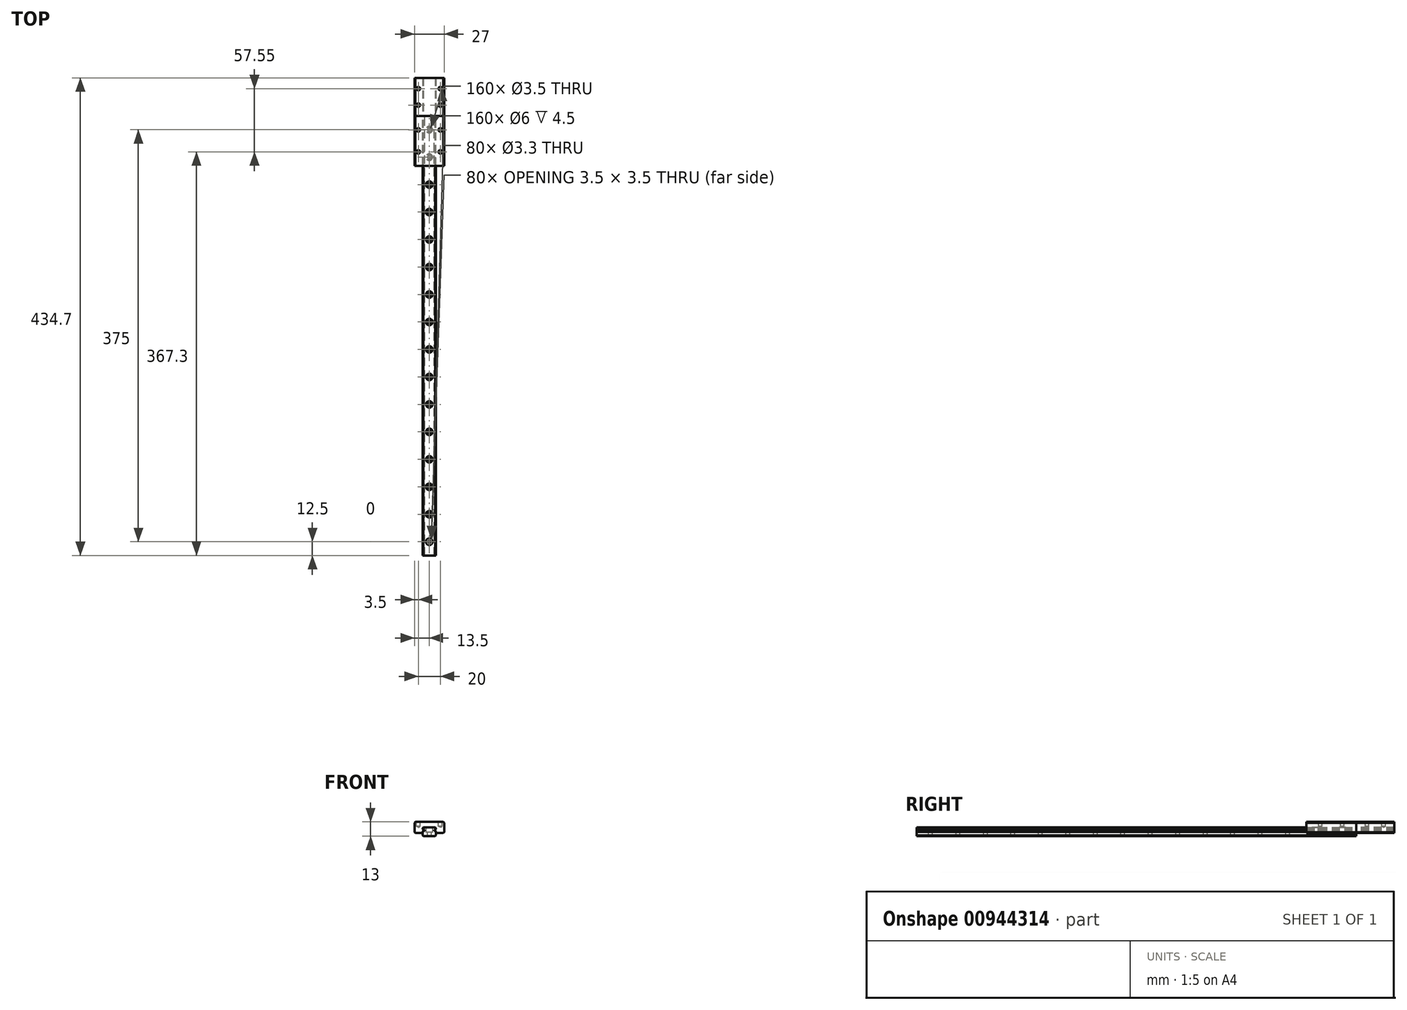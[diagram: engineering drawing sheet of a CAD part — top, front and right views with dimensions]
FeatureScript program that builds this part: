
annotation { "Feature Type Name" : "Feature", "Feature Type Description" : "" }
export const myFeature = defineFeature(function(context is Context, id is Id, definition is map)
    precondition{}
    {
        {
            var Q0;
            Q0=qCreatedBy(makeId("Front.planeOp"),FACE);
            var sketch = newSketch(context, id + "F0", { "sketchPlane" : qUnion([Q0])});
            skLineSegment(sketch, "E0.bottom", {"start": v(5.3, -4) * mm, "end": v(-5.3, -4) * mm});
            skLineSegment(sketch, "E0.top", {"start": v(5.3, 4) * mm, "end": v(-5.3, 4) * mm});
            skLineSegment(sketch, "E0.left", {"start": v(6, -3.3) * mm, "end": v(6, 0.09) * mm});
            skLineSegment(sketch, "E0.right", {"start": v(-6, -3.3) * mm, "end": v(-6, 0.09) * mm});
            skPoint(sketch, "E0.middle", {"position": v(0, 0) * mm});
            skLineSegment(sketch, "E1", {"start": v(0, 12.36) * mm, "end": v(0, -9.73) * mm, "construction": true});
            skLineSegment(sketch, "E2", {"start": v(-6, 2.5) * mm, "end": v(-5.3, 1.8) * mm});
            skLineSegment(sketch, "E3", {"start": v(-5.3, 1.8) * mm, "end": v(-4.3, 1.8) * mm});
            skLineSegment(sketch, "E4", {"start": v(-4.3, 1.8) * mm, "end": v(-4.3, 0.8) * mm});
            skLineSegment(sketch, "E5", {"start": v(-4.3, 0.8) * mm, "end": v(-5.3, 0.8) * mm});
            skLineSegment(sketch, "E6", {"start": v(-5.3, 0.8) * mm, "end": v(-6, 0.09) * mm});
            skLineSegment(sketch, "E7.MirrorCS", {"start": v(4.3, 0.8) * mm, "end": v(5.3, 0.8) * mm});
            skLineSegment(sketch, "E8.MirrorCS", {"start": v(5.3, 0.8) * mm, "end": v(6, 0.09) * mm});
            skLineSegment(sketch, "E9.MirrorCS", {"start": v(4.3, 1.8) * mm, "end": v(4.3, 0.8) * mm});
            skLineSegment(sketch, "E10.MirrorCS", {"start": v(6, 2.5) * mm, "end": v(5.3, 1.8) * mm});
            skLineSegment(sketch, "E11.MirrorCS", {"start": v(5.3, 1.8) * mm, "end": v(4.3, 1.8) * mm});
            skLineSegment(sketch, "E12.trimOffspring", {"start": v(-6, 2.5) * mm, "end": v(-6, 3.3) * mm});
            skLineSegment(sketch, "E13.trimOffspring", {"start": v(6, 2.5) * mm, "end": v(6, 3.3) * mm});
            skLineSegment(sketch, "E14", {"start": v(-6, 3.3) * mm, "end": v(-5.3, 4) * mm});
            skLineSegment(sketch, "E15.MirrorCS", {"start": v(6, 3.3) * mm, "end": v(5.3, 4) * mm});
            skLineSegment(sketch, "E16.MirrorCS", {"start": v(-6, -3.3) * mm, "end": v(-5.3, -4) * mm});
            skLineSegment(sketch, "E17.MirrorCS", {"start": v(6, -3.3) * mm, "end": v(5.3, -4) * mm});
            skPoint(sketch, "E18.orphan", {"position": v(-6, 4) * mm});
            skPoint(sketch, "E19.orphan", {"position": v(6, 4) * mm});
            skPoint(sketch, "E20.orphan", {"position": v(6, -4) * mm});
            skPoint(sketch, "E21.orphan", {"position": v(-6, -4) * mm});
            skSolve(sketch);
        }
        {
            var Q0;
            Q0=makeQuery(id+"F0.imprint","IMPRINT",FACE,{"disambiguationData":[TD([[makeQuery(id+"F0.imprint","IMPRINT",EDGE,{"derivedFrom":sQuery(id+"F0.wireOp",EDGE,"E0.bottom")}),-1.0]])]});
            extrude(context, id + "F1", {"entities" : qUnion([Q0]), "depth" : 400 * mm, "offsetDistance" : 25 * mm});
        }
        {
            var Q0;
            Q0=makeQuery(id+"F1.opExtrude","SWEPT_FACE",FACE,{"disambiguationData":[OSD([sQuery(id+"F0.wireOp",EDGE,"E0.top")])]});
            var sketch = newSketch(context, id + "F2", { "sketchPlane" : qUnion([Q0])});
            skLineSegment(sketch, "E22", {"start": v(0, 4.61) * mm, "end": v(0, -375.08) * mm, "construction": true});
            skCircle(sketch, "E23", {"center": v(0, -12.5) * mm, "radius": 1.75 * mm});
            skCircle(sketch, "E24.1.0.0", {"center": v(0, -37.5) * mm, "radius": 1.75 * mm});
            skCircle(sketch, "E24.2.0.0", {"center": v(0, -62.5) * mm, "radius": 1.75 * mm});
            skCircle(sketch, "E24.3.0.0", {"center": v(0, -87.5) * mm, "radius": 1.75 * mm});
            skCircle(sketch, "E24.4.0.0", {"center": v(0, -112.5) * mm, "radius": 1.75 * mm});
            skCircle(sketch, "E24.5.0.0", {"center": v(0, -137.5) * mm, "radius": 1.75 * mm});
            skCircle(sketch, "E24.6.0.0", {"center": v(0, -162.5) * mm, "radius": 1.75 * mm});
            skCircle(sketch, "E24.7.0.0", {"center": v(0, -187.5) * mm, "radius": 1.75 * mm});
            skCircle(sketch, "E24.8.0.0", {"center": v(0, -212.5) * mm, "radius": 1.75 * mm});
            skLineSegment(sketch, "E24.direction1", {"start": v(0, -12.5) * mm, "end": v(0, -37.5) * mm, "construction": true});
            skCircle(sketch, "E25.0.9.0", {"center": v(0, -237.5) * mm, "radius": 1.75 * mm});
            skCircle(sketch, "E25.0.10.0", {"center": v(0, -262.5) * mm, "radius": 1.75 * mm});
            skCircle(sketch, "E25.0.11.0", {"center": v(0, -287.5) * mm, "radius": 1.75 * mm});
            skCircle(sketch, "E25.0.12.0", {"center": v(0, -312.5) * mm, "radius": 1.75 * mm});
            skCircle(sketch, "E25.0.13.0", {"center": v(0, -337.5) * mm, "radius": 1.75 * mm});
            skCircle(sketch, "E26.0.14.0", {"center": v(0, -362.5) * mm, "radius": 1.75 * mm});
            skCircle(sketch, "E26.0.15.0", {"center": v(0, -387.5) * mm, "radius": 1.75 * mm});
            skSolve(sketch);
        }
        {
            var Q0;
            Q0=qSketchRegion(id+"F2",true);
            extrude(context, id + "F3", {"entities" : qUnion([Q0]), "operationType" : NewBodyOperationType.REMOVE, "endBound" : BoundingType.THROUGH_ALL, "oppositeDirection" : true, "depth" : 25 * mm, "offsetDistance" : 25 * mm});
        }
        {
            var Q0;
            Q0=makeQuery(id+"F1.opExtrude","SWEPT_FACE",FACE,{"disambiguationData":[OSD([sQuery(id+"F0.wireOp",EDGE,"E0.top")])]});
            var sketch = newSketch(context, id + "F4", { "sketchPlane" : qUnion([Q0])});
            skLineSegment(sketch, "E27", {"start": v(0, 167.82) * mm, "end": v(0, -211.88) * mm, "construction": true});
            skCircle(sketch, "E28", {"center": v(0, -12.5) * mm, "radius": 3 * mm});
            skCircle(sketch, "E29.1.0.0", {"center": v(0, -37.5) * mm, "radius": 3 * mm});
            skCircle(sketch, "E29.2.0.0", {"center": v(0, -62.5) * mm, "radius": 3 * mm});
            skCircle(sketch, "E29.3.0.0", {"center": v(0, -87.5) * mm, "radius": 3 * mm});
            skCircle(sketch, "E29.4.0.0", {"center": v(0, -112.5) * mm, "radius": 3 * mm});
            skCircle(sketch, "E29.5.0.0", {"center": v(0, -137.5) * mm, "radius": 3 * mm});
            skCircle(sketch, "E29.6.0.0", {"center": v(0, -162.5) * mm, "radius": 3 * mm});
            skCircle(sketch, "E29.7.0.0", {"center": v(0, -187.5) * mm, "radius": 3 * mm});
            skCircle(sketch, "E29.8.0.0", {"center": v(0, -212.5) * mm, "radius": 3 * mm});
            skLineSegment(sketch, "E29.direction1", {"start": v(0, -12.5) * mm, "end": v(0, -37.5) * mm, "construction": true});
            skCircle(sketch, "E30.0.9.0", {"center": v(0, -237.5) * mm, "radius": 3 * mm});
            skCircle(sketch, "E30.0.10.0", {"center": v(0, -262.5) * mm, "radius": 3 * mm});
            skCircle(sketch, "E30.0.11.0", {"center": v(0, -287.5) * mm, "radius": 3 * mm});
            skCircle(sketch, "E30.0.12.0", {"center": v(0, -312.5) * mm, "radius": 3 * mm});
            skCircle(sketch, "E30.0.13.0", {"center": v(0, -337.5) * mm, "radius": 3 * mm});
            skCircle(sketch, "E31.0.14.0", {"center": v(0, -362.5) * mm, "radius": 3 * mm});
            skCircle(sketch, "E31.0.15.0", {"center": v(0, -387.5) * mm, "radius": 3 * mm});
            skSolve(sketch);
        }
        {
            var Q0;
            Q0=qSketchRegion(id+"F4",true);
            extrude(context, id + "F5", {"entities" : qUnion([Q0]), "operationType" : NewBodyOperationType.REMOVE, "oppositeDirection" : true, "depth" : 4.5 * mm, "offsetDistance" : 25 * mm});
        }
        {
            var Q0;
            Q0=qCreatedBy(makeId("Front.planeOp"),FACE);
            var sketch = newSketch(context, id + "F6", { "sketchPlane" : qUnion([Q0])});
            skLineSegment(sketch, "E32", {"start": v(-6.15, -1) * mm, "end": v(-12.8, -1) * mm});
            skLineSegment(sketch, "E33", {"start": v(-13.5, -0.3) * mm, "end": v(-13.5, 8.3) * mm});
            skLineSegment(sketch, "E34", {"start": v(-12.8, 9) * mm, "end": v(0, 9) * mm});
            skLineSegment(sketch, "E35", {"start": v(-6.15, -1) * mm, "end": v(-6.15, 0.15) * mm});
            skLineSegment(sketch, "E36", {"start": v(-6.15, 0.15) * mm, "end": v(-5.3, 1) * mm});
            skLineSegment(sketch, "E37", {"start": v(-5.3, 1) * mm, "end": v(-5.3, 1.58) * mm});
            skLineSegment(sketch, "E38", {"start": v(-5.3, 1.58) * mm, "end": v(-6.15, 2.44) * mm});
            skLineSegment(sketch, "E39", {"start": v(-6.15, 2.44) * mm, "end": v(-6.15, 3.36) * mm});
            skLineSegment(sketch, "E40", {"start": v(-6.15, 3.36) * mm, "end": v(-5.36, 4.15) * mm});
            skLineSegment(sketch, "E41", {"start": v(-5.36, 4.15) * mm, "end": v(0, 4.15) * mm});
            skLineSegment(sketch, "E42", {"start": v(-13.5, 8.3) * mm, "end": v(-12.8, 9) * mm});
            skLineSegment(sketch, "E43", {"start": v(-12.8, -1) * mm, "end": v(-13.5, -0.3) * mm});
            skPoint(sketch, "E44.orphan", {"position": v(-13.5, -1) * mm});
            skPoint(sketch, "E45.orphan", {"position": v(-13.5, 9) * mm});
            skLineSegment(sketch, "E46.MirrorCS", {"start": v(12.8, 9) * mm, "end": v(0, 9) * mm});
            skLineSegment(sketch, "E47.MirrorCS", {"start": v(13.5, 8.3) * mm, "end": v(12.8, 9) * mm});
            skLineSegment(sketch, "E48.MirrorCS", {"start": v(13.5, -0.3) * mm, "end": v(13.5, 8.3) * mm});
            skLineSegment(sketch, "E49.MirrorCS", {"start": v(12.8, -1) * mm, "end": v(13.5, -0.3) * mm});
            skLineSegment(sketch, "E50.MirrorCS", {"start": v(6.15, -1) * mm, "end": v(12.8, -1) * mm});
            skLineSegment(sketch, "E51.MirrorCS", {"start": v(6.15, -1) * mm, "end": v(6.15, 0.15) * mm});
            skLineSegment(sketch, "E52.MirrorCS", {"start": v(6.15, 0.15) * mm, "end": v(5.3, 1) * mm});
            skLineSegment(sketch, "E53.MirrorCS", {"start": v(5.3, 1) * mm, "end": v(5.3, 1.58) * mm});
            skLineSegment(sketch, "E54.MirrorCS", {"start": v(5.3, 1.58) * mm, "end": v(6.15, 2.44) * mm});
            skLineSegment(sketch, "E55.MirrorCS", {"start": v(6.15, 2.44) * mm, "end": v(6.15, 3.36) * mm});
            skLineSegment(sketch, "E56.MirrorCS", {"start": v(6.15, 3.36) * mm, "end": v(5.36, 4.15) * mm});
            skLineSegment(sketch, "E57.MirrorCS", {"start": v(5.36, 4.15) * mm, "end": v(0, 4.15) * mm});
            skSolve(sketch);
        }
        {
            var Q0;
            Q0=qSketchRegion(id+"F6",true);
            extrude(context, id + "F7", {"entities" : qUnion([Q0]), "depth" : 45.4 * mm, "offsetDistance" : 25 * mm});
        }
        {
            var Q0;
            Q0=qSketchRegion(id+"F6",true);
            extrude(context, id + "F8", {"entities" : qUnion([Q0]), "oppositeDirection" : true, "depth" : 34.7 * mm, "offsetDistance" : 25 * mm});
        }
        {
            var Q0;
            Q0=makeQuery(id+"F7.opExtrude","SWEPT_FACE",FACE,{"disambiguationData":[OSD([sQuery(id+"F6.wireOp",EDGE,"E34"),sQuery(id+"F6.wireOp",EDGE,"E46.MirrorCS")])]});
            var sketch = newSketch(context, id + "F9", { "sketchPlane" : qUnion([Q0])});
            skLineSegment(sketch, "E58", {"start": v(-12.8, 0) * mm, "end": v(12.8, -45.4) * mm, "construction": true});
            skLineSegment(sketch, "E59", {"start": v(12.8, 0) * mm, "end": v(-12.8, -45.4) * mm, "construction": true});
            skLineSegment(sketch, "E60", {"start": v(-37.81, -22.7) * mm, "end": v(32.35, -22.7) * mm, "construction": true});
            skPoint(sketch, "E60.startSnap0", {"position": v(0, -22.7) * mm});
            skLineSegment(sketch, "E61", {"start": v(0, 0) * mm, "end": v(0, -61.52) * mm, "construction": true});
            skCircle(sketch, "E62", {"center": v(-10, -12.7) * mm, "radius": 1.5 * mm});
            skCircle(sketch, "E63.MirrorC", {"center": v(10, -12.7) * mm, "radius": 1.5 * mm});
            skCircle(sketch, "E64.MirrorC", {"center": v(-10, -32.7) * mm, "radius": 1.5 * mm});
            skCircle(sketch, "E65.MirrorC", {"center": v(10, -32.7) * mm, "radius": 1.5 * mm});
            skSolve(sketch);
        }
        {
            var Q0;
            Q0=makeQuery(id+"F8.opExtrude","SWEPT_FACE",FACE,{"disambiguationData":[OSD([sQuery(id+"F6.wireOp",EDGE,"E34"),sQuery(id+"F6.wireOp",EDGE,"E46.MirrorCS")])]});
            var sketch = newSketch(context, id + "F10", { "sketchPlane" : qUnion([Q0])});
            skLineSegment(sketch, "E66", {"start": v(-34.35, 17.35) * mm, "end": v(28.23, 17.35) * mm, "construction": true});
            skLineSegment(sketch, "E67", {"start": v(0, 49.38) * mm, "end": v(0, -1.77) * mm, "construction": true});
            skCircle(sketch, "E68", {"center": v(-10, 24.85) * mm, "radius": 1.5 * mm});
            skCircle(sketch, "E69.MirrorC", {"center": v(10, 24.85) * mm, "radius": 1.5 * mm});
            skCircle(sketch, "E70.MirrorC", {"center": v(-10, 9.85) * mm, "radius": 1.5 * mm});
            skCircle(sketch, "E71.MirrorC", {"center": v(10, 9.85) * mm, "radius": 1.5 * mm});
            skSolve(sketch);
        }
        {
            var Q0;
            Q0=sQuery(id+"F9.wireOp",VERTEX,"E62.center");
            var Q1;
            Q1=sQuery(id+"F9.wireOp",VERTEX,"E63.MirrorC.center");
            var Q2;
            Q2=sQuery(id+"F9.wireOp",VERTEX,"E64.MirrorC.center");
            var Q3;
            Q3=sQuery(id+"F9.wireOp",VERTEX,"E65.MirrorC.center");
            var Q4;
            Q4=makeQuery(id+"F7.opExtrude","SWEPT_BODY",BODY,{"disambiguationData":[OSD([sQuery(id+"F6.wireOp",EDGE,"E32"),sQuery(id+"F6.wireOp",EDGE,"E33"),sQuery(id+"F6.wireOp",EDGE,"E34"),sQuery(id+"F6.wireOp",EDGE,"E35"),sQuery(id+"F6.wireOp",EDGE,"E36"),sQuery(id+"F6.wireOp",EDGE,"E37"),sQuery(id+"F6.wireOp",EDGE,"E38"),sQuery(id+"F6.wireOp",EDGE,"E39"),sQuery(id+"F6.wireOp",EDGE,"E40"),sQuery(id+"F6.wireOp",EDGE,"E41"),sQuery(id+"F6.wireOp",EDGE,"E42"),sQuery(id+"F6.wireOp",EDGE,"E43"),sQuery(id+"F6.wireOp",EDGE,"E46.MirrorCS"),sQuery(id+"F6.wireOp",EDGE,"E47.MirrorCS"),sQuery(id+"F6.wireOp",EDGE,"E48.MirrorCS"),sQuery(id+"F6.wireOp",EDGE,"E49.MirrorCS"),sQuery(id+"F6.wireOp",EDGE,"E50.MirrorCS"),sQuery(id+"F6.wireOp",EDGE,"E51.MirrorCS"),sQuery(id+"F6.wireOp",EDGE,"E52.MirrorCS"),sQuery(id+"F6.wireOp",EDGE,"E53.MirrorCS"),sQuery(id+"F6.wireOp",EDGE,"E54.MirrorCS"),sQuery(id+"F6.wireOp",EDGE,"E55.MirrorCS"),sQuery(id+"F6.wireOp",EDGE,"E56.MirrorCS"),sQuery(id+"F6.wireOp",EDGE,"E57.MirrorCS")])]});
            hole(context, id + "F11", {"style" : HoleStyle.SIMPLE, "endStyle" : HoleEndStyle.BLIND, "standardTappedOrClearance" : lookupTablePath({ "standard" : "ISO", "fit" : "Normal", "size" : "M3", "type" : "Clearance" }), "standardBlindInLast" : lookupTablePath({ "fit" : "Standard", "standard" : "ISO", "size" : "M3", "type" : "Clearance" }), "holeDiameter" : 3.3 * mm, "majorDiameter" : 5 * mm, "holeDepth" : 4 * mm, "isTappedThrough" : true, "tappedDepth" : 12 * mm, "tapClearance" : 3, "startFromSketch" : true, "locations" : qUnion([Q0, Q1, Q2, Q3]), "scope" : qUnion([Q4])});
        }
        {
            var Q0;
            Q0=sQuery(id+"F10.wireOp",VERTEX,"E68.center");
            var Q1;
            Q1=sQuery(id+"F10.wireOp",VERTEX,"E69.MirrorC.center");
            var Q2;
            Q2=sQuery(id+"F10.wireOp",VERTEX,"E71.MirrorC.center");
            var Q3;
            Q3=sQuery(id+"F10.wireOp",VERTEX,"E70.MirrorC.center");
            var Q4;
            Q4=makeQuery(id+"F8.opExtrude","SWEPT_BODY",BODY,{"disambiguationData":[OSD([sQuery(id+"F6.wireOp",EDGE,"E32"),sQuery(id+"F6.wireOp",EDGE,"E33"),sQuery(id+"F6.wireOp",EDGE,"E34"),sQuery(id+"F6.wireOp",EDGE,"E35"),sQuery(id+"F6.wireOp",EDGE,"E36"),sQuery(id+"F6.wireOp",EDGE,"E37"),sQuery(id+"F6.wireOp",EDGE,"E38"),sQuery(id+"F6.wireOp",EDGE,"E39"),sQuery(id+"F6.wireOp",EDGE,"E40"),sQuery(id+"F6.wireOp",EDGE,"E41"),sQuery(id+"F6.wireOp",EDGE,"E42"),sQuery(id+"F6.wireOp",EDGE,"E43"),sQuery(id+"F6.wireOp",EDGE,"E46.MirrorCS"),sQuery(id+"F6.wireOp",EDGE,"E47.MirrorCS"),sQuery(id+"F6.wireOp",EDGE,"E48.MirrorCS"),sQuery(id+"F6.wireOp",EDGE,"E49.MirrorCS"),sQuery(id+"F6.wireOp",EDGE,"E50.MirrorCS"),sQuery(id+"F6.wireOp",EDGE,"E51.MirrorCS"),sQuery(id+"F6.wireOp",EDGE,"E52.MirrorCS"),sQuery(id+"F6.wireOp",EDGE,"E53.MirrorCS"),sQuery(id+"F6.wireOp",EDGE,"E54.MirrorCS"),sQuery(id+"F6.wireOp",EDGE,"E55.MirrorCS"),sQuery(id+"F6.wireOp",EDGE,"E56.MirrorCS"),sQuery(id+"F6.wireOp",EDGE,"E57.MirrorCS")])]});
            hole(context, id + "F12", {"style" : HoleStyle.SIMPLE, "endStyle" : HoleEndStyle.BLIND, "standardTappedOrClearance" : lookupTablePath({ "standard" : "ISO", "fit" : "Normal", "size" : "M3", "type" : "Clearance" }), "standardBlindInLast" : lookupTablePath({ "fit" : "Standard", "standard" : "ISO", "size" : "M3", "type" : "Clearance" }), "holeDiameter" : 3.3 * mm, "majorDiameter" : 5 * mm, "holeDepth" : 4 * mm, "isTappedThrough" : true, "tappedDepth" : 12 * mm, "tapClearance" : 3, "startFromSketch" : true, "locations" : qUnion([Q0, Q1, Q2, Q3]), "scope" : qUnion([Q4])});
        }
    });
